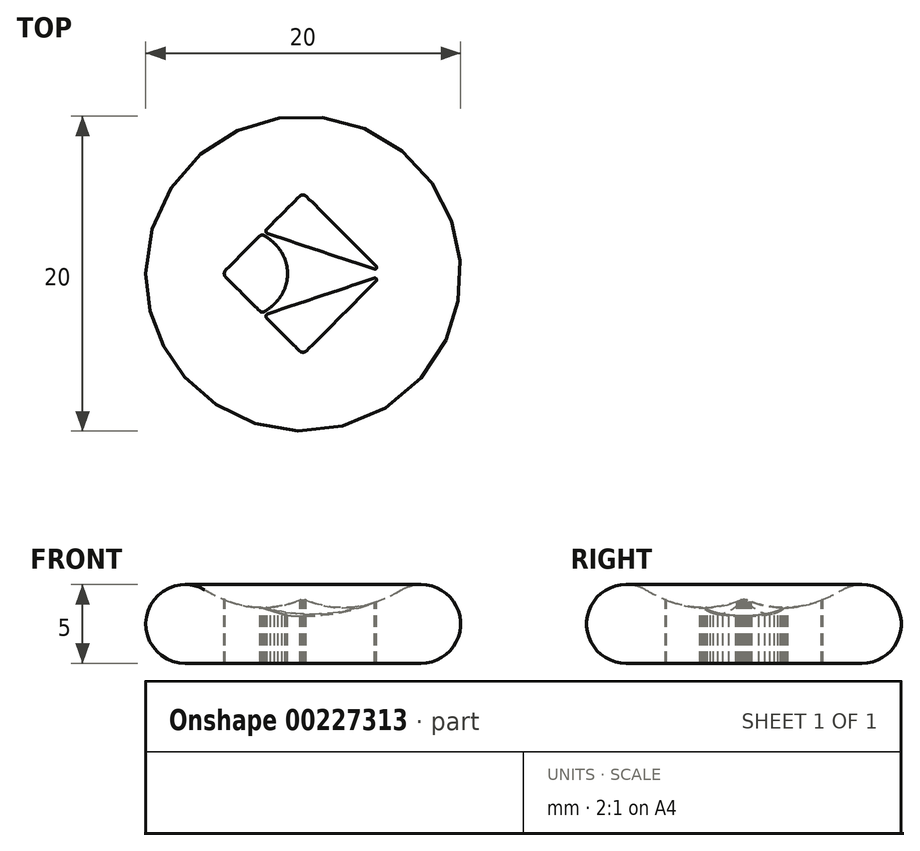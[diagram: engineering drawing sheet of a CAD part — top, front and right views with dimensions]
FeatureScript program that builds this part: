
annotation { "Feature Type Name" : "Feature", "Feature Type Description" : "" }
export const myFeature = defineFeature(function(context is Context, id is Id, definition is map)
    precondition{}
    {
        {
            var Q0;
            Q0=qCreatedBy(makeId("Front.planeOp"),FACE);
            var sketch = newSketch(context, id + "F0", { "sketchPlane" : qUnion([Q0])});
            skCircle(sketch, "E0", {"center": v(-7.5, 2.5) * mm, "radius": 2.5 * mm});
            skLineSegment(sketch, "E1", {"start": v(-7.5, 0) * mm, "end": v(0, 0) * mm});
            skLineSegment(sketch, "E2", {"start": v(0, 0) * mm, "end": v(0, 3) * mm});
            skArc(sketch, "E3", {"start": v(-6.26, 4.67) * mm, "mid": v(-3.24, 3.42) * mm, "end": v(0, 3) * mm});
            skPoint(sketch, "E4", {"position": v(-7.5, 0) * mm});
            skSolve(sketch);
        }
        {
            var Q0;
            Q0 = qSketchRegion(id + "F0", true);
            var Q1;
            Q1=sQuery(id+"F0.wireOp",EDGE,"E2");
            revolve(context, id + "F1", {"entities" : qUnion([Q0]), "axis" : qUnion([Q1]), "revolveType" : RevolveType.FULL});
        }
        {
            var Q0;
            Q0=qCreatedBy(makeId("Top.planeOp"),FACE);
            cPlane(context, id + "F2", {"entities" : qUnion([Q0]), "cplaneType" : CPlaneType.OFFSET, "offset" : 15 * mm, "width" : 150 * mm, "height" : 150 * mm});
        }
        {
            var Q0;
            Q0=qCreatedBy(id+"F2.planeOp",FACE);
            var sketch = newSketch(context, id + "F3", { "sketchPlane" : qUnion([Q0])});
            skLineSegment(sketch, "E5", {"start": v(4.64, 0.47) * mm, "end": v(0.2, 4.91) * mm});
            skLineSegment(sketch, "E6", {"start": v(0.2, 4.91) * mm, "end": v(0.18, 4.93) * mm});
            skLineSegment(sketch, "E7", {"start": v(0.18, 4.93) * mm, "end": v(0.1, 4.98) * mm});
            skLineSegment(sketch, "E8", {"start": v(0.1, 4.98) * mm, "end": v(-0.01, 5) * mm});
            skLineSegment(sketch, "E9", {"start": v(-0.01, 5) * mm, "end": v(-0.13, 4.98) * mm});
            skLineSegment(sketch, "E10", {"start": v(-0.13, 4.98) * mm, "end": v(-0.2, 4.93) * mm});
            skLineSegment(sketch, "E11", {"start": v(-0.2, 4.93) * mm, "end": v(-0.23, 4.91) * mm});
            skLineSegment(sketch, "E12", {"start": v(-0.23, 4.91) * mm, "end": v(-2.33, 2.81) * mm});
            skLineSegment(sketch, "E13", {"start": v(-2.33, 2.81) * mm, "end": v(-2.34, 2.8) * mm});
            skLineSegment(sketch, "E14", {"start": v(-2.34, 2.8) * mm, "end": v(-2.37, 2.74) * mm});
            skLineSegment(sketch, "E15", {"start": v(-2.37, 2.74) * mm, "end": v(-2.37, 2.66) * mm});
            skLineSegment(sketch, "E16", {"start": v(-2.37, 2.66) * mm, "end": v(-2.34, 2.6) * mm});
            skLineSegment(sketch, "E17", {"start": v(-2.34, 2.6) * mm, "end": v(-2.29, 2.56) * mm});
            skLineSegment(sketch, "E18", {"start": v(-2.29, 2.56) * mm, "end": v(-2.27, 2.55) * mm});
            skLineSegment(sketch, "E19", {"start": v(-2.27, 2.55) * mm, "end": v(4.52, 0.28) * mm});
            skLineSegment(sketch, "E20", {"start": v(4.52, 0.28) * mm, "end": v(4.54, 0.28) * mm});
            skLineSegment(sketch, "E21", {"start": v(4.54, 0.28) * mm, "end": v(4.6, 0.29) * mm});
            skLineSegment(sketch, "E22", {"start": v(4.6, 0.29) * mm, "end": v(4.66, 0.33) * mm});
            skLineSegment(sketch, "E23", {"start": v(4.66, 0.33) * mm, "end": v(4.67, 0.4) * mm});
            skLineSegment(sketch, "E24", {"start": v(4.67, 0.4) * mm, "end": v(4.65, 0.46) * mm});
            skLineSegment(sketch, "E25", {"start": v(4.65, 0.46) * mm, "end": v(4.64, 0.47) * mm});
            skLineSegment(sketch, "E26", {"start": v(-2.32, -2.82) * mm, "end": v(-0.23, -4.91) * mm});
            skLineSegment(sketch, "E27", {"start": v(-0.23, -4.91) * mm, "end": v(-0.21, -4.93) * mm});
            skLineSegment(sketch, "E28", {"start": v(-0.21, -4.93) * mm, "end": v(-0.13, -4.98) * mm});
            skLineSegment(sketch, "E29", {"start": v(-0.13, -4.98) * mm, "end": v(-0.01, -5) * mm});
            skLineSegment(sketch, "E30", {"start": v(-0.01, -5) * mm, "end": v(0.1, -4.98) * mm});
            skLineSegment(sketch, "E31", {"start": v(0.1, -4.98) * mm, "end": v(0.18, -4.93) * mm});
            skLineSegment(sketch, "E32", {"start": v(0.18, -4.93) * mm, "end": v(0.2, -4.91) * mm});
            skLineSegment(sketch, "E33", {"start": v(0.2, -4.91) * mm, "end": v(4.64, -0.47) * mm});
            skLineSegment(sketch, "E34", {"start": v(4.64, -0.47) * mm, "end": v(4.65, -0.46) * mm});
            skLineSegment(sketch, "E35", {"start": v(4.65, -0.46) * mm, "end": v(4.67, -0.4) * mm});
            skLineSegment(sketch, "E36", {"start": v(4.67, -0.4) * mm, "end": v(4.66, -0.33) * mm});
            skLineSegment(sketch, "E37", {"start": v(4.66, -0.33) * mm, "end": v(4.6, -0.29) * mm});
            skLineSegment(sketch, "E38", {"start": v(4.6, -0.29) * mm, "end": v(4.54, -0.28) * mm});
            skLineSegment(sketch, "E39", {"start": v(4.54, -0.28) * mm, "end": v(4.52, -0.29) * mm});
            skLineSegment(sketch, "E40", {"start": v(4.52, -0.29) * mm, "end": v(-2.26, -2.56) * mm});
            skLineSegment(sketch, "E41", {"start": v(-2.26, -2.56) * mm, "end": v(-2.28, -2.56) * mm});
            skLineSegment(sketch, "E42", {"start": v(-2.28, -2.56) * mm, "end": v(-2.33, -2.6) * mm});
            skLineSegment(sketch, "E43", {"start": v(-2.33, -2.6) * mm, "end": v(-2.37, -2.67) * mm});
            skLineSegment(sketch, "E44", {"start": v(-2.37, -2.67) * mm, "end": v(-2.36, -2.75) * mm});
            skLineSegment(sketch, "E45", {"start": v(-2.36, -2.75) * mm, "end": v(-2.34, -2.8) * mm});
            skLineSegment(sketch, "E46", {"start": v(-2.34, -2.8) * mm, "end": v(-2.32, -2.82) * mm});
            skLineSegment(sketch, "E47", {"start": v(-0.99, 0) * mm, "end": v(-0.99, 0.13) * mm});
            skLineSegment(sketch, "E48", {"start": v(-0.99, 0.13) * mm, "end": v(-1.03, 0.5) * mm});
            skLineSegment(sketch, "E49", {"start": v(-1.03, 0.5) * mm, "end": v(-1.16, 0.95) * mm});
            skLineSegment(sketch, "E50", {"start": v(-1.16, 0.95) * mm, "end": v(-1.35, 1.33) * mm});
            skLineSegment(sketch, "E51", {"start": v(-1.35, 1.33) * mm, "end": v(-1.58, 1.66) * mm});
            skLineSegment(sketch, "E52", {"start": v(-1.58, 1.66) * mm, "end": v(-1.83, 1.93) * mm});
            skLineSegment(sketch, "E53", {"start": v(-1.83, 1.93) * mm, "end": v(-2.08, 2.15) * mm});
            skLineSegment(sketch, "E54", {"start": v(-2.08, 2.15) * mm, "end": v(-2.3, 2.31) * mm});
            skLineSegment(sketch, "E55", {"start": v(-2.3, 2.31) * mm, "end": v(-2.44, 2.4) * mm});
            skLineSegment(sketch, "E56", {"start": v(-2.44, 2.4) * mm, "end": v(-2.48, 2.42) * mm});
            skLineSegment(sketch, "E57", {"start": v(-2.48, 2.42) * mm, "end": v(-2.5, 2.44) * mm});
            skLineSegment(sketch, "E58", {"start": v(-2.5, 2.44) * mm, "end": v(-2.63, 2.45) * mm});
            skLineSegment(sketch, "E59", {"start": v(-2.63, 2.45) * mm, "end": v(-2.74, 2.4) * mm});
            skLineSegment(sketch, "E60", {"start": v(-2.74, 2.4) * mm, "end": v(-2.76, 2.39) * mm});
            skLineSegment(sketch, "E61", {"start": v(-2.76, 2.39) * mm, "end": v(-4.92, 0.22) * mm});
            skLineSegment(sketch, "E62", {"start": v(-4.92, 0.22) * mm, "end": v(-4.95, 0.2) * mm});
            skLineSegment(sketch, "E63", {"start": v(-4.95, 0.2) * mm, "end": v(-5, 0.12) * mm});
            skLineSegment(sketch, "E64", {"start": v(-5, 0.12) * mm, "end": v(-5.01, 0) * mm});
            skLineSegment(sketch, "E65", {"start": v(-5.01, 0) * mm, "end": v(-5, -0.11) * mm});
            skLineSegment(sketch, "E66", {"start": v(-5, -0.11) * mm, "end": v(-4.95, -0.2) * mm});
            skLineSegment(sketch, "E67", {"start": v(-4.95, -0.2) * mm, "end": v(-4.92, -0.22) * mm});
            skLineSegment(sketch, "E68", {"start": v(-4.92, -0.22) * mm, "end": v(-2.75, -2.39) * mm});
            skLineSegment(sketch, "E69", {"start": v(-2.75, -2.39) * mm, "end": v(-2.73, -2.4) * mm});
            skLineSegment(sketch, "E70", {"start": v(-2.73, -2.4) * mm, "end": v(-2.62, -2.45) * mm});
            skLineSegment(sketch, "E71", {"start": v(-2.62, -2.45) * mm, "end": v(-2.5, -2.44) * mm});
            skLineSegment(sketch, "E72", {"start": v(-2.5, -2.44) * mm, "end": v(-2.48, -2.42) * mm});
            skLineSegment(sketch, "E73", {"start": v(-2.48, -2.42) * mm, "end": v(-2.43, -2.4) * mm});
            skLineSegment(sketch, "E74", {"start": v(-2.43, -2.4) * mm, "end": v(-2.3, -2.3) * mm});
            skLineSegment(sketch, "E75", {"start": v(-2.3, -2.3) * mm, "end": v(-2.07, -2.15) * mm});
            skLineSegment(sketch, "E76", {"start": v(-2.07, -2.15) * mm, "end": v(-1.83, -1.93) * mm});
            skLineSegment(sketch, "E77", {"start": v(-1.83, -1.93) * mm, "end": v(-1.58, -1.66) * mm});
            skLineSegment(sketch, "E78", {"start": v(-1.58, -1.66) * mm, "end": v(-1.35, -1.33) * mm});
            skLineSegment(sketch, "E79", {"start": v(-1.35, -1.33) * mm, "end": v(-1.16, -0.95) * mm});
            skLineSegment(sketch, "E80", {"start": v(-1.16, -0.95) * mm, "end": v(-1.03, -0.5) * mm});
            skLineSegment(sketch, "E81", {"start": v(-1.03, -0.5) * mm, "end": v(-0.99, -0.13) * mm});
            skLineSegment(sketch, "E82", {"start": v(-0.99, -0.13) * mm, "end": v(-0.99, 0) * mm});
            skSolve(sketch);
        }
        {
            var Q0;
            Q0 = qSketchRegion(id + "F3", true);
            extrude(context, id + "F4", {"entities" : qUnion([Q0]), "operationType" : NewBodyOperationType.REMOVE, "oppositeDirection" : true, "depth" : 20 * mm});
        }
    });
